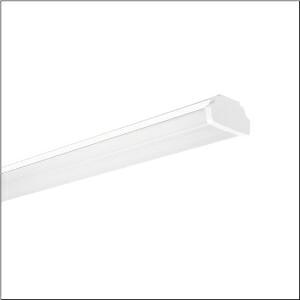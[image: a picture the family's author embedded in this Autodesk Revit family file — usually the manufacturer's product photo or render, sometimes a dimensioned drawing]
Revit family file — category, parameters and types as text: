
# Revit family: modario_r__31_mo_53bm812c1v4075_06f5
name_source: partatom
category: Lighting Fixtures
units: mm (PartAtom-declared; Revit-internal decimal feet)

## family parameters
Cut with Voids When Loaded = No
Host = Face
Light Source = No
Part Type = Normal
Room Calculation Point = No
Round Connector Dimension = Use Diameter
Shared = No

## types (1)
- --- (1 x LED, 7620 lm, 48.9 W, 4000K)
    Apparent Load = 49 VA
    CIE Flux Codes = 47 80 95 92 100
    Color Rendering = 80
    Color Temperature = 4000K
    Default Elevation = 1800 mm
    Description = Modario® 31 MO, luminaire insert, of sheet steel, coil coated, white, length: 1.495mm, width: 81mm, height: 82mm, 5x system unit, system units: 299mm, LED rated luminous flux: 7.620lm, light colour: 840, control gear: ON/OFF Multilumen, CLOi, control gear: ECG Multilumen, with plug, 3-pole, with phase selection, mains connection: 220..240V, AC, 50/60Hz, start of lifetime: 49W, end of service life: 56W, through-wiring accessed according to module size, primary optical cover: cover, of PMMA, light emission: direct distribution, primary light characteristic: symmetric, protection rating (complete): IP20, protection rating (LED compartment): IP50, insulation class (complete): insulation class I (protective earthing), certification: CE, ENEC, VDE, UKCA, impact resistance: IK03, permissible ambient temperature for indoor applications: -35..+30°C, corresponds to IFS (International Featured Standards) requirements for safety and quality in the food industry, reducing of maximum allowable ambient temperature of 5°C with ceiling mounting, packaging unit: 1 piece
    Height = 92 mm
    Lamp = 1 x LED
    Lamp Light Flux = 7620 lm
    Lamp Power = 48.9 W
    Lamp count = 1
    Length = 1495 mm
    Luminous efficacy = 156 lm/W
    Manufacturer = Siteco
    ModVariant = No
    Model = 53BM812C1V4075
    Mounting Place = Ceiling
    Mounting Type = Pendant
    Number of Poles = 1
    OnlyDefault = Yes
    Power Factor = 1
    Product Name = Modario® 31 MO
    Product group = luminaire insert
    ProductGroupID = 901
    Protection Class = Protection class I
    Protection Degree = IP 20
    RLX_Detail_Level = 1
    RLX_Emergency_Light_Flux = 0 lm
    RLX_Emergency_Type = 0
    RLX_Emergency_Type_DB = No
    RlxData = <blob elided: 40061 chars, md5=1f5cf5b6>
    Socket = socket
    Standby Power = 0 W
    System Light Flux = 7620 lm
    System Power = 49 W
    Type Comments = factory setting: luminous flux: 100 % | (A | C | E) | 107 mA
    Type Image = l_1300283.jpg
    URL = http://relux.com
    VarID = @adj_155019
    Voltage = 0 V
    Weight = 0.00 kg
    Width = 81 mm

## geometry (parser evidence)
native form markers: Blend x4, Sweep x12
no freeform markers — native parametric forms only
